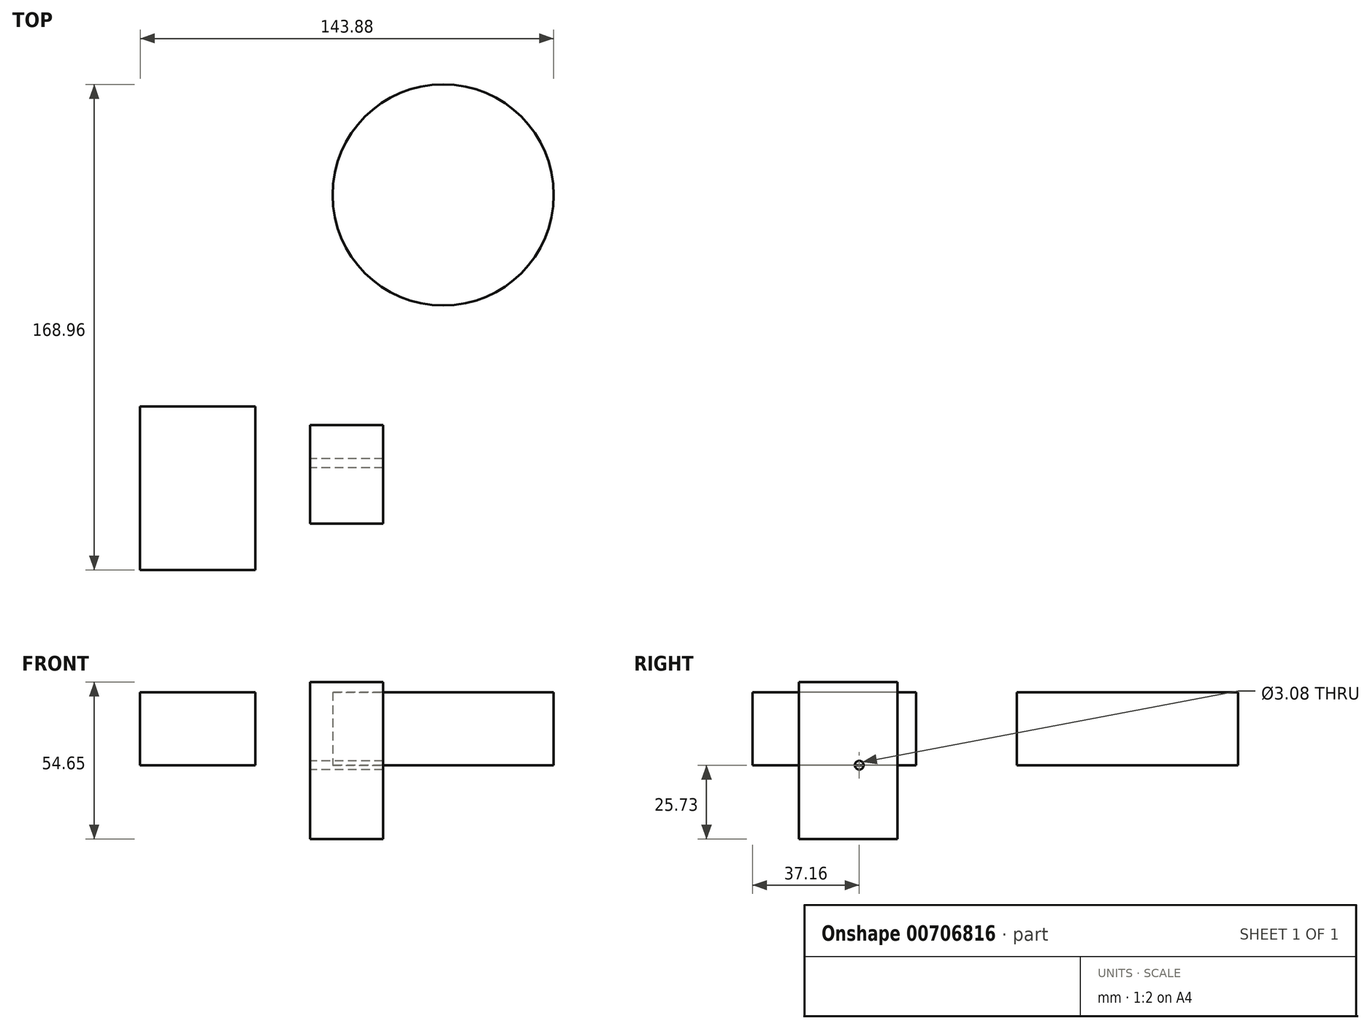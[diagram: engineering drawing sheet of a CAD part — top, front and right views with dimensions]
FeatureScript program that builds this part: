
annotation { "Feature Type Name" : "Feature", "Feature Type Description" : "" }
export const myFeature = defineFeature(function(context is Context, id is Id, definition is map)
    precondition{}
    {
        {
            var Q0;
            Q0=qCreatedBy(makeId("Right.planeOp"),FACE);
            var sketch = newSketch(context, id + "F0", { "sketchPlane" : qUnion([Q0])});
            skCircle(sketch, "E0", {"center": v(0, 0) * mm, "radius": 1.54 * mm});
            skLineSegment(sketch, "E1.bottom", {"start": v(13.32, 28.92) * mm, "end": v(-21, 28.92) * mm});
            skLineSegment(sketch, "E1.top", {"start": v(13.32, -25.73) * mm, "end": v(-21, -25.73) * mm});
            skLineSegment(sketch, "E1.left", {"start": v(13.32, 28.92) * mm, "end": v(13.32, -25.73) * mm});
            skLineSegment(sketch, "E1.right", {"start": v(-21, 28.92) * mm, "end": v(-21, -25.73) * mm});
            skSolve(sketch);
        }
        {
            var Q0;
            Q0 = qSketchRegion(id + "F0", true);
            extrude(context, id + "F1", {"entities" : qUnion([Q0]), "depth" : 25.4 * mm, "offsetDistance" : 25.4 * mm});
        }
        {
            var Q0;
            Q0=qCreatedBy(makeId("Top.planeOp"),FACE);
            var sketch = newSketch(context, id + "F2", { "sketchPlane" : qUnion([Q0])});
            skLineSegment(sketch, "E2.bottom", {"start": v(-59.1, 19.8) * mm, "end": v(-19.06, 19.8) * mm});
            skLineSegment(sketch, "E2.top", {"start": v(-59.1, -37.16) * mm, "end": v(-19.06, -37.16) * mm});
            skLineSegment(sketch, "E2.left", {"start": v(-59.1, 19.8) * mm, "end": v(-59.1, -37.16) * mm});
            skLineSegment(sketch, "E2.right", {"start": v(-19.06, 19.8) * mm, "end": v(-19.06, -37.16) * mm});
            skPoint(sketch, "E2.middle", {"position": v(-39.08, -8.68) * mm});
            skSolve(sketch);
        }
        {
            var Q0;
            Q0=makeQuery(id+"F2.imprint","IMPRINT",FACE,{"disambiguationData":[TD([[makeQuery(id+"F2.imprint","IMPRINT",EDGE,{"derivedFrom":sQuery(id+"F2.wireOp",EDGE,"E2.bottom")}),-1.0]])]});
            extrude(context, id + "F3", {"entities" : qUnion([Q0]), "depth" : 25.4 * mm, "offsetDistance" : 25.4 * mm});
        }
        {
            var Q0;
            Q0=qCreatedBy(makeId("Top.planeOp"),FACE);
            var sketch = newSketch(context, id + "F4", { "sketchPlane" : qUnion([Q0])});
            skLineSegment(sketch, "E3.bottom", {"start": v(72.35, 46.94) * mm, "end": v(21.38, 46.94) * mm});
            skLineSegment(sketch, "E3.top", {"start": v(72.35, 137.97) * mm, "end": v(21.38, 137.97) * mm});
            skLineSegment(sketch, "E3.left", {"start": v(72.35, 46.94) * mm, "end": v(72.35, 137.97) * mm});
            skLineSegment(sketch, "E3.right", {"start": v(21.38, 46.94) * mm, "end": v(21.38, 137.97) * mm});
            skPoint(sketch, "E3.middle", {"position": v(46.87, 92.46) * mm});
            skLineSegment(sketch, "E4.bottom", {"start": v(81.16, -38.32) * mm, "end": v(124.35, -38.32) * mm});
            skLineSegment(sketch, "E4.top", {"start": v(81.16, 51.6) * mm, "end": v(124.35, 51.6) * mm});
            skLineSegment(sketch, "E4.left", {"start": v(81.16, -38.32) * mm, "end": v(81.16, 51.6) * mm});
            skLineSegment(sketch, "E4.right", {"start": v(124.35, -38.32) * mm, "end": v(124.35, 51.6) * mm});
            skPoint(sketch, "E4.middle", {"position": v(102.75, 6.64) * mm});
            skSolve(sketch);
        }
        {
            var Q0;
            Q0=makeQuery(id+"F4.imprint","IMPRINT",FACE,{"disambiguationData":[TD([[makeQuery(id+"F4.imprint","IMPRINT",EDGE,{"derivedFrom":sQuery(id+"F4.wireOp",EDGE,"E3.bottom")}),-1.0]])]});
            var sketch = newSketch(context, id + "F5", { "sketchPlane" : qUnion([Q0])});
            skCircle(sketch, "E5", {"center": v(46.32, 93.32) * mm, "radius": 38.47 * mm});
            skSolve(sketch);
        }
        {
            var Q0;
            Q0 = qSketchRegion(id + "F5", true);
            extrude(context, id + "F6", {"entities" : qUnion([Q0]), "depth" : 25.4 * mm, "offsetDistance" : 25.4 * mm});
        }
    });
